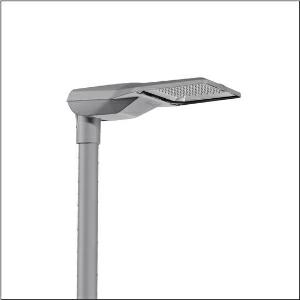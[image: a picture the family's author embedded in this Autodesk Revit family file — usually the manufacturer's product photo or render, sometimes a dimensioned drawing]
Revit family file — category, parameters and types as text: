
# Revit family: streetlight_sl_21_iq_midi___st1_0a_5xe3d41d08mb_7520
name_source: partatom
category: Lighting Fixtures
units: mm (PartAtom-declared; Revit-internal decimal feet)

## family parameters
Cut with Voids When Loaded = No
Host = Face
Light Source = No
Part Type = Normal
Room Calculation Point = No
Round Connector Dimension = Use Diameter
Shared = No

## types (1)
- --- (1 x LED, 20360 lm, 146.7 W, 4000K)
    Apparent Load = 147 VA
    CIE Flux Codes = 37 72 97 100 100
    Color Rendering = 70
    Color Temperature = 4000K
    Default Elevation = 1800 mm
    Description = Streetlight SL 21 iQ midi, mast luminaire, primary light control with lens, of PMMA, primary optical cover: cover, of toughened safety glass, transparent, light distribution: ST1.0a, light emission: direct distribution, primary light characteristic: asymmetric, installation type: post-top, side-entry, LED, High Power LED, rated luminous flux: 20.360lm, luminous efficacy: 139lm/W, light colour: 740, colour temperature: 4000K, control: Auto-Match, Temp-Guard, Lumen-Switch, Night-Set, Smart-Wire, Light-Fading, Desk-Remote (wireless, voltage-free reading and setting of iQ features in the workshop via application-optimized NFC function/RFID function), optimised constant luminous flux control (CLO 2.0), presetting dimming linear, mains connection: 230..240V, AC, 50/60Hz, start of lifetime: 147W, end of service life: 161W, reduction: 62W, luminaire housing, of diecast aluminium, powder-coated, Siteco® metallic grey (DB 702S), corrosivity category C5 mid according to DIN EN ISO 12944, please order mast flange separately, inclination adjustable: 0°, 5°, 10°, 15°, sealing non-destructively replaceable, multi-level sealing system, length: 644mm, width: 335mm, height: 110mm, mast flange for spigot size: 42mm (side-entry): 5XC10008XM4, 60/48mm (side-entry/post-top): 5XC10108XM2, 76/60mm (side-entry/post-top): 5XC10108XM1, protection rating (complete): IP66, insulation class (complete): insulation class II (safety insulation), certification: CE, ENEC, ENEC+, VDE, impact resistance: IK09, permissible operating ambient temperature for outdoor applications: -40..+50°C, standard-compliant lighting for roads and squares, packaging unit: 1 piece

Light Distribution: ST1.0a
    Height = 111 mm
    Lamp = 1 x LED
    Lamp Light Flux = 20360 lm
    Lamp Power = 146.7 W
    Lamp count = 1
    Length = 644 mm
    Luminous efficacy = 139 lm/W
    Manufacturer = Siteco
    ModVariant = No
    Model = 5XE3D41D08MB
    Number of Poles = 1
    OnlyDefault = Yes
    Power Factor = 1
    Product Name = Streetlight SL 21 iQ midi | ST1.0a
    Product group = mast luminaire | pylon top
    ProductGroupID = 6100
    Protection Class = Protection class II
    Protection Degree = IP 66
    RLX_Detail_Level = 1
    RLX_Emergency_Light_Flux = 0 lm
    RLX_Emergency_Type = 0
    RLX_Emergency_Type_DB = No
    RlxData = <blob elided: 90625 chars, md5=986a177d>
    Socket = socket
    Standby Power = 0 W
    System Light Flux = 20360 lm
    System Power = 147 W
    Type Comments = factory setting: luminous flux: 100 % | dim-lin: 254 | 753 mA
    Type Image = l_1004298.jpg
    URL = http://relux.com
    VarID = @adj_123449
    Voltage = 0 V
    Weight = 0.00 kg
    Width = 336 mm

## geometry (parser evidence)
native form markers: Blend x4, Sweep x12
no freeform markers — native parametric forms only
